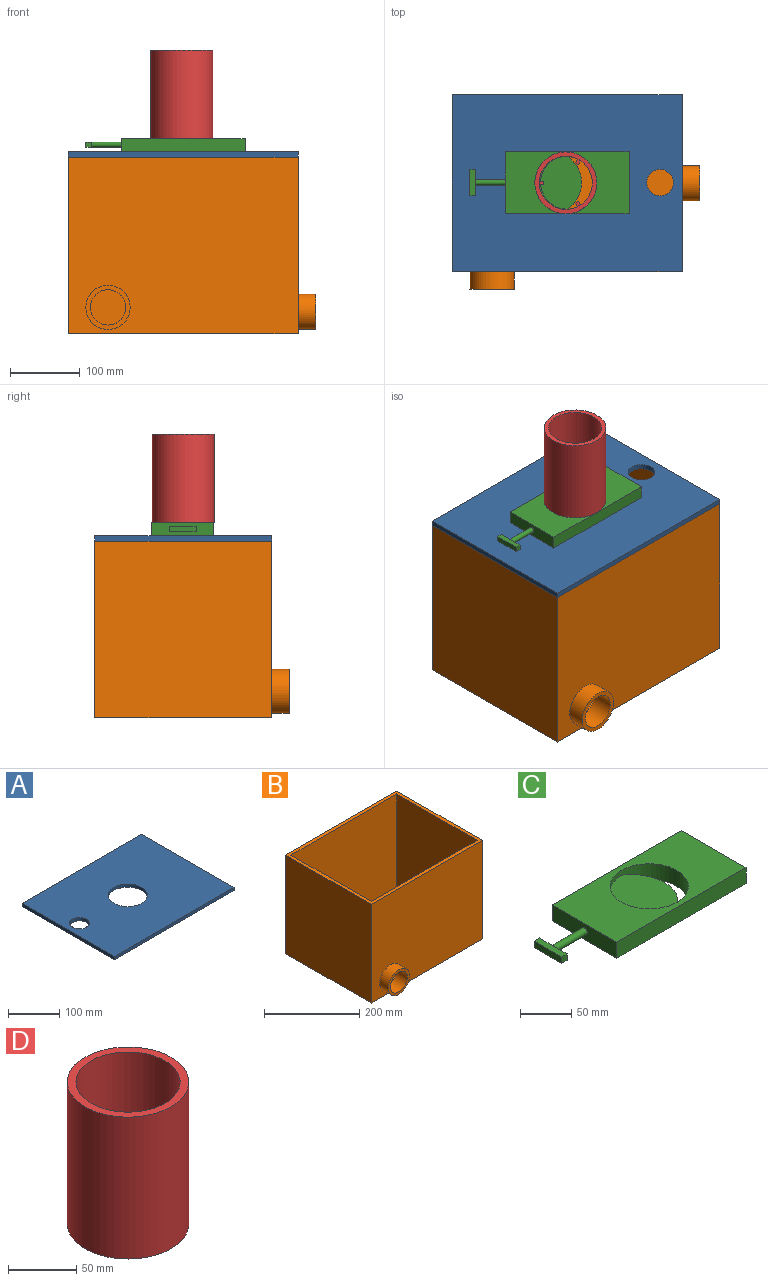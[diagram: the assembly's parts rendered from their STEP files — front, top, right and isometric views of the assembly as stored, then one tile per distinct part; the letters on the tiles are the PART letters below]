
ASSEMBLY  parts=4 mates=7
PART A: 8 faces, bbox 330.2x254x7.6 mm
  f0: plane 254x7.62mm, normal (1,0,0), area 1935.5mm2, adj f1,f3,f4,f5
  f1: plane 330.2x7.62mm, normal (0,1,0), area 2516.1mm2, adj f0,f2,f4,f5
  f2: plane 254x7.62mm, normal (-1,0,0), area 1935.5mm2, adj f1,f3,f4,f5
  f3: plane 330.2x7.62mm, normal (0,-1,0), area 2516.1mm2, adj f0,f2,f4,f5
  f4: plane 330.2x254mm, normal (0,0,1), area 78170.3mm2, adj f0,f1,f2,f3,f6,f7
  f5: plane 330.2x254mm, normal (0,0,-1), area 78170.3mm2, adj f0,f1,f2,f3,f6,f7
  f6: cylinder r=38.1mm len=76.2mm, axis (0,0,1), area 1824.1mm2, adj f4,f5
  f7: cylinder r=19.05mm len=38.1mm, axis (0,0,1), area 912.1mm2, adj f4,f5
PART B: 17 faces, bbox 355.6x279.4x254 mm
  f0: plane 330.2x254mm, normal (0,0,1), area 8671mm2, adj f1,f2,f3,f4,f6,f7,f8,f9
  f1: plane 254x254mm, normal (1,0,0), area 62489.2mm2, adj f0,f2,f4,f5,f11
  f2: plane 330.2x254mm, normal (0,1,0), area 83870.8mm2, adj f0,f1,f3,f5
  f3: plane 254x254mm, normal (-1,0,0), area 64516mm2, adj f0,f2,f4,f5
  f4: plane 330.2x254mm, normal (0,-1,0), area 80703.9mm2, adj f0,f1,f3,f5,f14
  f5: plane 330.2x254mm, normal (0,0,-1), area 83870.8mm2, adj f1,f2,f3,f4
  f6: plane 246.38x238.76mm, normal (-1,0,0), area 57685.6mm2, adj f0,f7,f9,f10,f13
  f7: plane 314.96x246.38mm, normal (0,-1,0), area 77599.8mm2, adj f0,f6,f8,f10
  f8: plane 246.38x238.76mm, normal (1,0,0), area 58825.7mm2, adj f0,f7,f9,f10
  f9: plane 314.96x246.38mm, normal (0,1,0), area 75573mm2, adj f0,f6,f8,f10,f16
  f10: plane 314.96x238.76mm, normal (0,0,1), area 75199.8mm2, adj f6,f7,f8,f9
  f11: cylinder r=25.4mm len=50.8mm, axis (-1,0,0), area 4053.7mm2, adj f1,f12
  f12: plane 50.8x50.8mm, normal (1,0,0), area 886.7mm2, adj f11,f13
  f13: cylinder r=19.05mm len=38.1mm, axis (1,0,0), area 3952.3mm2, adj f6,f12
  f14: cylinder r=31.75mm len=63.5mm, axis (0,1,0), area 5067.1mm2, adj f4,f15
  f15: plane 63.5x63.5mm, normal (0,-1,0), area 1140.1mm2, adj f14,f16
  f16: cylinder r=25.4mm len=50.8mm, axis (0,-1,0), area 5269.8mm2, adj f9,f15
PART C: 20 faces, bbox 228.6x88.9x19.1 mm
  f0: cylinder r=3.81mm len=43.18mm, axis (1,0,0), area 1033.7mm2, adj f3,f17,f19
  f1: plane 88.9x19.05mm, normal (1,0,0), area 1693.5mm2, adj f2,f4,f5,f6
  f2: plane 177.8x19.05mm, normal (0,1,0), area 3387.1mm2, adj f1,f3,f5,f6
  f3: plane 88.9x19.05mm, normal (-1,0,0), area 1647.9mm2, adj f0,f2,f4,f5,f6
  f4: plane 177.8x19.05mm, normal (0,-1,0), area 3387.1mm2, adj f1,f3,f5,f6
  f5: plane 177.8x88.9mm, normal (0,0,1), area 11246.1mm2, adj f1,f2,f3,f4,f7
  f6: plane 177.8x88.9mm, normal (0,0,-1), area 11246.1mm2, adj f1,f2,f3,f4,f7
  f7: cylinder r=38.1mm len=76.2mm, axis (0,0,1), area 3666.3mm2, adj f5,f6,f8,f9,f10,f11
  f8: plane 7.62x1.18mm, normal (0,1,0), area 9mm2, adj f7,f10,f11,f12
  f9: plane 7.62x1.18mm, normal (0,-1,0), area 9mm2, adj f7,f10,f11,f12
  f10: plane 76.16x58.89mm, normal (0,0,1), area 3396.1mm2, adj f7,f8,f9,f12
  f11: plane 76.16x58.89mm, normal (0,0,-1), area 3396.1mm2, adj f7,f8,f9,f12
  f12: cylinder r=45.28mm len=76.16mm, axis (0,0,-1), area 689.5mm2, adj f8,f9,f10,f11
  f13: plane 38.1x7.62mm, normal (-1,0,0), area 290.3mm2, adj f14,f15,f16,f18
  f14: plane 38.1x7.62mm, normal (0,0,1), area 290.3mm2, adj f13,f15,f17,f18,f19
  f15: plane 7.62x7.62mm, normal (0,1,0), area 58.1mm2, adj f13,f14,f16,f17
  f16: plane 38.1x7.62mm, normal (0,0,-1), area 290.3mm2, adj f13,f15,f17,f18,f19
  f17: plane 19.05x7.62mm, normal (1,0,0), area 122.4mm2, adj f0,f14,f15,f16
  f18: plane 7.62x7.62mm, normal (0,-1,0), area 58.1mm2, adj f13,f14,f16,f19
  f19: plane 19.05x7.62mm, normal (1,0,0), area 122.4mm2, adj f0,f14,f16,f18
PART D: 16 faces, bbox 88.9x88.9x127 mm
  f0: cylinder r=38.1mm len=127mm, axis (0,0,-1), area 30245.1mm2, adj f2,f3,f4,f5,f7,f8,f9,f11
  f1: cylinder r=44.45mm len=127mm, axis (0,0,-1), area 35469.5mm2, adj f2,f3
  f2: plane 88.9x88.9mm, normal (0,0,1), area 1646.8mm2, adj f0,f1
  f3: plane 88.9x88.9mm, normal (0,0,-1), area 1744.6mm2, adj f0,f1,f5,f6,f7,f9,f10,f11
  f4: plane 6.35x5.16mm, normal (0,0,1), area 32.6mm2, adj f0,f5,f6,f7
  f5: plane 10.16x6.26mm, normal (0,-1,0), area 63.6mm2, adj f0,f3,f4,f6
  f6: plane 10.16x5.16mm, normal (1,0,0), area 52.4mm2, adj f3,f4,f5,f7
  f7: plane 10.16x6.26mm, normal (0,1,0), area 63.6mm2, adj f0,f3,f4,f6
  f8: plane 8x7.6mm, normal (0,0,1), area 32.6mm2, adj f0,f9,f10,f11
  f9: plane 10.16x5.42mm, normal (0.87,0.5,0), area 63.6mm2, adj f0,f3,f8,f10
  f10: plane 10.16x4.47mm, normal (-0.5,0.87,0), area 52.4mm2, adj f3,f8,f9,f11
  f11: plane 10.16x5.42mm, normal (-0.87,-0.5,0), area 63.6mm2, adj f0,f3,f8,f10
  f12: plane 8x7.6mm, normal (0,0,1), area 32.6mm2, adj f0,f13,f14,f15
  f13: plane 10.16x5.42mm, normal (-0.87,0.5,0), area 63.6mm2, adj f0,f3,f12,f14
  f14: plane 10.16x4.47mm, normal (-0.5,-0.87,0), area 52.4mm2, adj f3,f12,f13,f15
  f15: plane 10.16x5.42mm, normal (0.87,-0.5,0), area 63.6mm2, adj f0,f3,f12,f14
PLACE A rot(axis=(0,-1,0),180deg) t=(165.07,-126.48,261.62)mm
PLACE B t=(165.1,-127,0)mm
PLACE C t=(165.07,-126.48,261.62)mm
PLACE D t=(163.16,-127.04,280.67)mm
MATE planar A.f2 <-> B.f1  axis (1,0,0) through (330.2,-127,257.81)mm
MATE planar D.f1 <-> C.f7  axis (0,0,-1) through (163.16,-127.04,280.67)mm
MATE cylindrical A.f6 <-> C.f7  axis (0,0,-1) through (165.07,-126.48,254)mm
MATE planar A.f3 <-> B.f4  axis (0,-1,0) through (165.1,-254,257.81)mm
MATE planar A.f5 <-> C.f7  axis (0,0,1) through (163.16,-127.04,261.62)mm
MATE planar A.f4 <-> B.f0  axis (0,0,-1) through (163.16,-127.04,254)mm
MATE cylindrical D.f0 <-> A.f5  axis (0,0,-1) through (163.16,-127.04,280.67)mm
